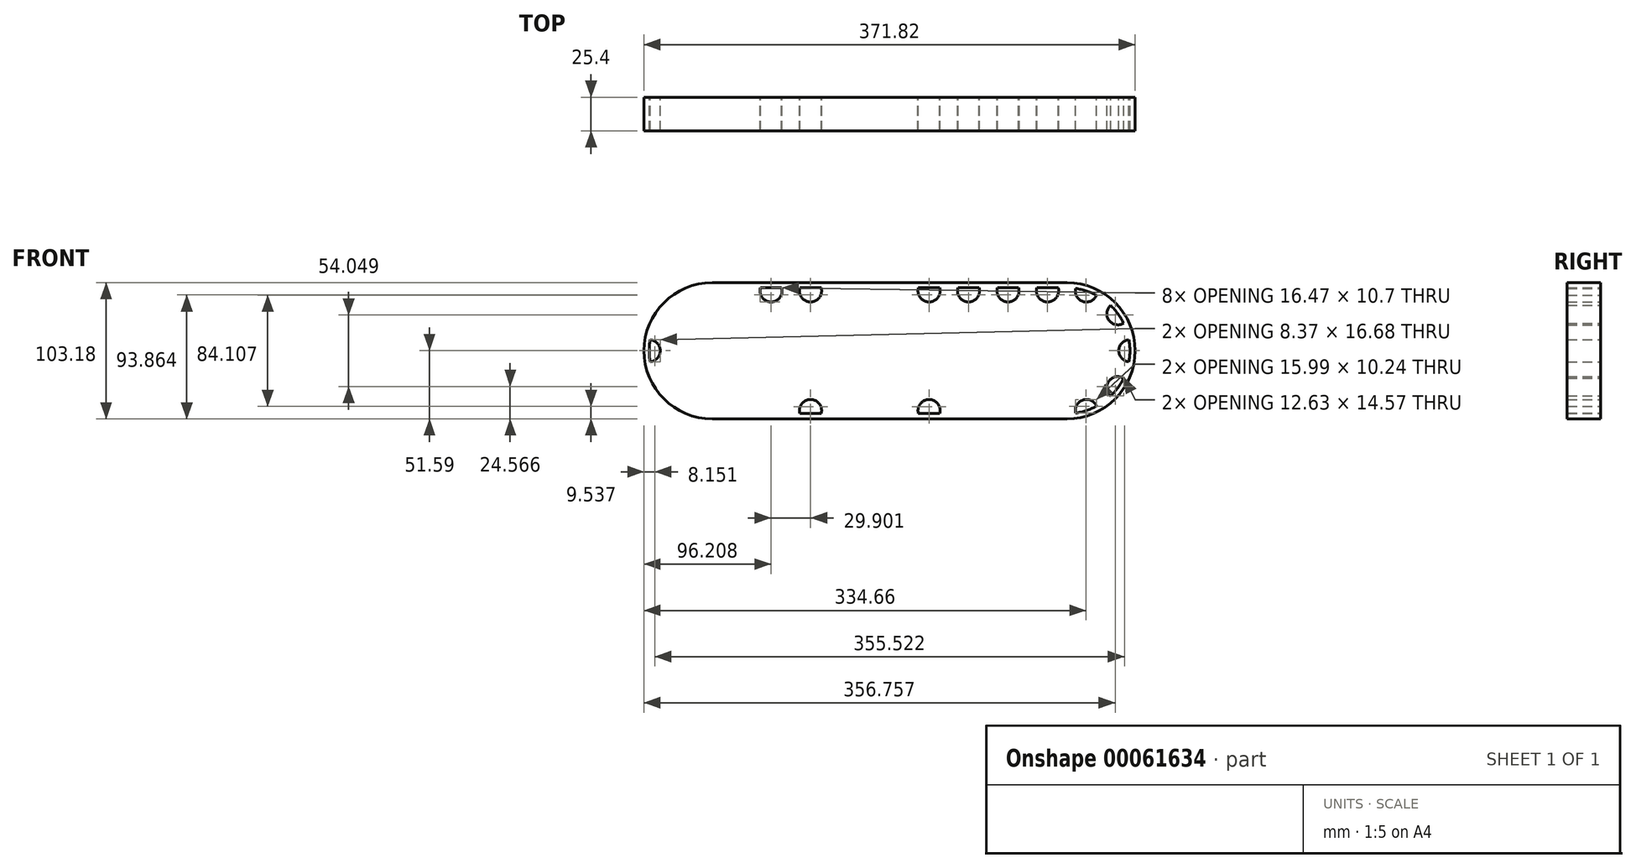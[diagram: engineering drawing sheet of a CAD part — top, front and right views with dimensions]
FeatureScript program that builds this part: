
annotation { "Feature Type Name" : "Feature", "Feature Type Description" : "" }
export const myFeature = defineFeature(function(context is Context, id is Id, definition is map)
    precondition{}
    {
        {
            var Q0;
            Q0=qCreatedBy(makeId("Front.planeOp"),FACE);
            var sketch = newSketch(context, id + "F0", { "sketchPlane" : qUnion([Q0])});
            skCircle(sketch, "E0", {"center": v(0, 0) * mm, "radius": 9.53 * mm});
            skCircle(sketch, "E1", {"center": v(0, 0) * mm, "radius": 15.88 * mm});
            skCircle(sketch, "E2", {"center": v(0, 0) * mm, "radius": 25.4 * mm});
            skCircle(sketch, "E3", {"center": v(0, 0) * mm, "radius": 38.1 * mm});
            skArc(sketch, "E4", {"start": v(5.87, 47.26) * mm, "mid": v(0, 47.63) * mm, "end": v(-5.87, 47.26) * mm});
            skLineSegment(sketch, "E5", {"start": v(-5.87, 47.26) * mm, "end": v(-7.62, 37.33) * mm});
            skLineSegment(sketch, "E6", {"start": v(5.87, 47.26) * mm, "end": v(7.62, 37.33) * mm});
            skLineSegment(sketch, "E7.1.0", {"start": v(-32.53, 34.79) * mm, "end": v(-28.1, 25.72) * mm});
            skArc(sketch, "E7.1.1", {"start": v(-23.03, 41.69) * mm, "mid": v(-28, 38.53) * mm, "end": v(-32.53, 34.79) * mm});
            skLineSegment(sketch, "E7.1.2", {"start": v(-23.03, 41.69) * mm, "end": v(-15.78, 34.68) * mm});
            skLineSegment(sketch, "E7.2.0", {"start": v(-46.76, 9.02) * mm, "end": v(-37.86, 4.29) * mm});
            skArc(sketch, "E7.2.1", {"start": v(-43.14, 20.19) * mm, "mid": v(-45.3, 14.72) * mm, "end": v(-46.76, 9.02) * mm});
            skLineSegment(sketch, "E7.2.2", {"start": v(-43.14, 20.19) * mm, "end": v(-33.15, 18.78) * mm});
            skLineSegment(sketch, "E7.3.0", {"start": v(-43.14, -20.19) * mm, "end": v(-33.15, -18.78) * mm});
            skArc(sketch, "E7.3.1", {"start": v(-46.76, -9.02) * mm, "mid": v(-45.3, -14.72) * mm, "end": v(-43.14, -20.19) * mm});
            skLineSegment(sketch, "E7.3.2", {"start": v(-46.76, -9.02) * mm, "end": v(-37.86, -4.29) * mm});
            skLineSegment(sketch, "E7.4.0", {"start": v(-23.03, -41.69) * mm, "end": v(-15.78, -34.68) * mm});
            skArc(sketch, "E7.4.1", {"start": v(-32.53, -34.79) * mm, "mid": v(-28, -38.53) * mm, "end": v(-23.03, -41.69) * mm});
            skLineSegment(sketch, "E7.4.2", {"start": v(-32.53, -34.79) * mm, "end": v(-28.1, -25.72) * mm});
            skLineSegment(sketch, "E7.5.0", {"start": v(5.87, -47.26) * mm, "end": v(7.62, -37.33) * mm});
            skArc(sketch, "E7.5.1", {"start": v(-5.87, -47.26) * mm, "mid": v(0, -47.63) * mm, "end": v(5.87, -47.26) * mm});
            skLineSegment(sketch, "E7.5.2", {"start": v(-5.87, -47.26) * mm, "end": v(-7.62, -37.33) * mm});
            skLineSegment(sketch, "E7.6.0", {"start": v(32.53, -34.79) * mm, "end": v(28.1, -25.72) * mm});
            skArc(sketch, "E7.6.1", {"start": v(23.03, -41.69) * mm, "mid": v(28, -38.53) * mm, "end": v(32.53, -34.79) * mm});
            skLineSegment(sketch, "E7.6.2", {"start": v(23.03, -41.69) * mm, "end": v(15.78, -34.68) * mm});
            skLineSegment(sketch, "E7.7.0", {"start": v(46.76, -9.02) * mm, "end": v(37.86, -4.29) * mm});
            skArc(sketch, "E7.7.1", {"start": v(43.14, -20.19) * mm, "mid": v(45.3, -14.72) * mm, "end": v(46.76, -9.02) * mm});
            skLineSegment(sketch, "E7.7.2", {"start": v(43.14, -20.19) * mm, "end": v(33.15, -18.78) * mm});
            skLineSegment(sketch, "E7.8.0", {"start": v(43.14, 20.19) * mm, "end": v(33.15, 18.78) * mm});
            skArc(sketch, "E7.8.1", {"start": v(46.76, 9.02) * mm, "mid": v(45.3, 14.72) * mm, "end": v(43.14, 20.19) * mm});
            skLineSegment(sketch, "E7.8.2", {"start": v(46.76, 9.02) * mm, "end": v(37.86, 4.29) * mm});
            skLineSegment(sketch, "E7.9.0", {"start": v(23.03, 41.69) * mm, "end": v(15.78, 34.68) * mm});
            skArc(sketch, "E7.9.1", {"start": v(32.53, 34.79) * mm, "mid": v(28, 38.53) * mm, "end": v(23.03, 41.69) * mm});
            skLineSegment(sketch, "E7.9.2", {"start": v(32.53, 34.79) * mm, "end": v(28.1, 25.72) * mm});
            skLineSegment(sketch, "E8", {"start": v(-3.98, 25.09) * mm, "end": v(-3.98, 15.37) * mm, "construction": true});
            skLineSegment(sketch, "E9", {"start": v(3.98, 25.09) * mm, "end": v(3.98, 15.37) * mm, "construction": true});
            skLineSegment(sketch, "E10.1.0", {"start": v(-19.74, -15.99) * mm, "end": v(-11.32, -11.13) * mm, "construction": true});
            skLineSegment(sketch, "E10.1.1", {"start": v(-23.71, -9.1) * mm, "end": v(-15.3, -4.24) * mm, "construction": true});
            skLineSegment(sketch, "E10.2.0", {"start": v(23.71, -9.1) * mm, "end": v(15.3, -4.24) * mm, "construction": true});
            skLineSegment(sketch, "E10.2.1", {"start": v(19.74, -15.99) * mm, "end": v(11.32, -11.13) * mm, "construction": true});
            skSolve(sketch);
        }
        {
            var Q0;
            Q0=qCreatedBy(makeId("Front.planeOp"),FACE);
            var sketch = newSketch(context, id + "F1", { "sketchPlane" : qUnion([Q0])});
            skArc(sketch, "E11", {"start": v(23.03, 41.69) * mm, "mid": v(-10.34, 46.49) * mm, "end": v(-38.53, 28) * mm});
            skLineSegment(sketch, "E12.0", {"start": v(5.87, 47.26) * mm, "end": v(7.62, 37.33) * mm, "construction": true});
            skLineSegment(sketch, "E12.1", {"start": v(23.03, 41.69) * mm, "end": v(15.78, 34.68) * mm, "construction": true});
            skLineSegment(sketch, "E12.2", {"start": v(-5.87, 47.26) * mm, "end": v(-7.62, 37.33) * mm, "construction": true});
            skLineSegment(sketch, "E12.3", {"start": v(-23.03, 41.69) * mm, "end": v(-15.78, 34.68) * mm, "construction": true});
            skLineSegment(sketch, "E12.4", {"start": v(-32.53, 34.79) * mm, "end": v(-28.1, 25.72) * mm, "construction": true});
            skLineSegment(sketch, "E12.5", {"start": v(-43.14, 20.19) * mm, "end": v(-33.15, 18.78) * mm, "construction": true});
            skLineSegment(sketch, "E12.6", {"start": v(-46.76, 9.02) * mm, "end": v(-37.86, 4.29) * mm, "construction": true});
            skLineSegment(sketch, "E12.7", {"start": v(-46.76, -9.02) * mm, "end": v(-37.86, -4.29) * mm, "construction": true});
            skCircle(sketch, "E13", {"center": v(-14.72, 45.3) * mm, "radius": 8.37 * mm});
            skCircle(sketch, "E14", {"center": v(-38.53, 28) * mm, "radius": 8.37 * mm});
            skCircle(sketch, "E15", {"center": v(-47.63, 0) * mm, "radius": 8.37 * mm});
            skCircle(sketch, "E16", {"center": v(14.72, 45.3) * mm, "radius": 8.37 * mm});
            skLineSegment(sketch, "E17", {"start": v(-14.72, 45.3) * mm, "end": v(14.72, 45.3) * mm, "construction": true});
            skArc(sketch, "E18.trimOffspring", {"start": v(-42.84, 20.81) * mm, "mid": v(-45.3, 14.72) * mm, "end": v(-46.89, 8.34) * mm});
            skArc(sketch, "E19.trimOffspring", {"start": v(-47.63, 0) * mm, "mid": v(-24.2, -41.02) * mm, "end": v(23.03, -41.69) * mm});
            skLineSegment(sketch, "E20", {"start": v(14.72, 45.3) * mm, "end": v(44.62, 45.3) * mm, "construction": true});
            skLineSegment(sketch, "E21", {"start": v(44.62, 45.3) * mm, "end": v(74.52, 45.3) * mm, "construction": true});
            skLineSegment(sketch, "E22", {"start": v(74.52, 45.3) * mm, "end": v(104.42, 45.3) * mm, "construction": true});
            skLineSegment(sketch, "E23", {"start": v(104.42, 45.3) * mm, "end": v(134.32, 45.3) * mm, "construction": true});
            skCircle(sketch, "E24", {"center": v(44.62, 45.3) * mm, "radius": 8.37 * mm});
            skCircle(sketch, "E25", {"center": v(74.52, 45.3) * mm, "radius": 8.37 * mm});
            skCircle(sketch, "E26", {"center": v(104.42, 45.3) * mm, "radius": 8.37 * mm});
            skCircle(sketch, "E27", {"center": v(134.32, 45.3) * mm, "radius": 8.37 * mm});
            skPoint(sketch, "E28", {"position": v(23.09, 45.3) * mm});
            skPoint(sketch, "E29", {"position": v(36.25, 45.3) * mm});
            skLineSegment(sketch, "E30", {"start": v(0, 0) * mm, "end": v(134.32, 0) * mm, "construction": true});
            skLineSegment(sketch, "E31", {"start": v(134.32, 45.3) * mm, "end": v(134.32, 0) * mm, "construction": true});
            skCircle(sketch, "E32.MirrorC", {"center": v(134.32, -45.3) * mm, "radius": 8.37 * mm});
            skCircle(sketch, "E33.MirrorC", {"center": v(104.42, -45.3) * mm, "radius": 8.37 * mm});
            skCircle(sketch, "E34.MirrorC", {"center": v(74.52, -45.3) * mm, "radius": 8.37 * mm});
            skCircle(sketch, "E35.MirrorC", {"center": v(44.62, -45.3) * mm, "radius": 8.37 * mm});
            skCircle(sketch, "E36.MirrorC", {"center": v(14.72, -45.3) * mm, "radius": 8.37 * mm});
            skCircle(sketch, "E37.MirrorC", {"center": v(-14.72, -45.3) * mm, "radius": 8.37 * mm});
            skCircle(sketch, "E38.MirrorC", {"center": v(-38.53, -28) * mm, "radius": 8.37 * mm});
            skCircle(sketch, "E39.MirrorC", {"center": v(164.22, 45.3) * mm, "radius": 8.37 * mm});
            skCircle(sketch, "E40.MirrorC", {"center": v(194.12, 45.3) * mm, "radius": 8.37 * mm});
            skCircle(sketch, "E41.MirrorC", {"center": v(224.03, 45.3) * mm, "radius": 8.37 * mm});
            skCircle(sketch, "E42.MirrorC", {"center": v(253.93, 45.3) * mm, "radius": 8.37 * mm});
            skCircle(sketch, "E43.MirrorC", {"center": v(283.36, 45.3) * mm, "radius": 8.37 * mm});
            skCircle(sketch, "E44.MirrorC", {"center": v(307.17, 28) * mm, "radius": 8.37 * mm});
            skCircle(sketch, "E45.MirrorC", {"center": v(316.27, 0) * mm, "radius": 8.37 * mm});
            skCircle(sketch, "E46.MirrorC", {"center": v(307.17, -28) * mm, "radius": 8.37 * mm});
            skCircle(sketch, "E47.MirrorC", {"center": v(283.36, -45.3) * mm, "radius": 8.37 * mm});
            skCircle(sketch, "E48.MirrorC", {"center": v(253.93, -45.3) * mm, "radius": 8.37 * mm});
            skCircle(sketch, "E49.MirrorC", {"center": v(224.03, -45.3) * mm, "radius": 8.37 * mm});
            skCircle(sketch, "E50.MirrorC", {"center": v(194.12, -45.3) * mm, "radius": 8.37 * mm});
            skCircle(sketch, "E51.MirrorC", {"center": v(164.22, -45.3) * mm, "radius": 8.37 * mm});
            skSolve(sketch);
        }
        {
            var Q0;
            Q0=qCreatedBy(makeId("Front.planeOp"),FACE);
            var sketch = newSketch(context, id + "F2", { "sketchPlane" : qUnion([Q0])});
            skArc(sketch, "E52", {"start": v(0, 47.63) * mm, "mid": v(-47.63, 0) * mm, "end": v(0, -47.63) * mm});
            skLineSegment(sketch, "E53", {"start": v(0, 47.63) * mm, "end": v(268.64, 47.63) * mm});
            skLineSegment(sketch, "E54", {"start": v(0, -47.63) * mm, "end": v(268.64, -47.63) * mm});
            skLineSegment(sketch, "E55.0", {"start": v(0, 0) * mm, "end": v(134.32, 0) * mm, "construction": true});
            skLineSegment(sketch, "E56.0", {"start": v(134.32, 45.3) * mm, "end": v(134.32, 0) * mm, "construction": true});
            skLineSegment(sketch, "E57.MirrorCS", {"start": v(268.64, 0) * mm, "end": v(134.32, 0) * mm, "construction": true});
            skArc(sketch, "E58", {"start": v(268.64, 47.62) * mm, "mid": v(316.27, 0) * mm, "end": v(268.64, -47.63) * mm});
            skLineSegment(sketch, "E59.0", {"start": v(0, 51.59) * mm, "end": v(268.64, 51.59) * mm});
            skArc(sketch, "E59.1", {"start": v(0, 51.59) * mm, "mid": v(-51.59, 0) * mm, "end": v(0, -51.59) * mm});
            skLineSegment(sketch, "E59.2", {"start": v(0, -51.59) * mm, "end": v(268.64, -51.59) * mm});
            skArc(sketch, "E59.3", {"start": v(268.64, 51.59) * mm, "mid": v(320.23, 0) * mm, "end": v(268.64, -51.59) * mm});
            skArc(sketch, "E60.0", {"start": v(-23.04, 46.15) * mm, "mid": v(-12.13, 37.33) * mm, "end": v(-8.49, 50.88) * mm});
            skArc(sketch, "E60.1", {"start": v(9.2, 51.59) * mm, "mid": v(14.72, 36.92) * mm, "end": v(20.24, 51.59) * mm});
            skArc(sketch, "E60.2", {"start": v(39.1, 51.59) * mm, "mid": v(44.62, 36.92) * mm, "end": v(50.14, 51.59) * mm});
            skArc(sketch, "E60.3", {"start": v(69, 51.59) * mm, "mid": v(74.52, 36.92) * mm, "end": v(80.04, 51.59) * mm});
            skArc(sketch, "E60.4", {"start": v(98.9, 51.59) * mm, "mid": v(102.07, 37.26) * mm, "end": v(112.46, 47.63) * mm});
            skArc(sketch, "E60.5", {"start": v(128.8, 51.59) * mm, "mid": v(134.32, 36.92) * mm, "end": v(139.84, 51.59) * mm});
            skArc(sketch, "E60.6", {"start": v(169.74, 51.59) * mm, "mid": v(164.22, 36.92) * mm, "end": v(158.7, 51.59) * mm});
            skArc(sketch, "E60.7", {"start": v(199.65, 51.59) * mm, "mid": v(194.12, 36.92) * mm, "end": v(188.6, 51.59) * mm});
            skArc(sketch, "E60.8", {"start": v(229.55, 51.59) * mm, "mid": v(224.03, 36.92) * mm, "end": v(218.5, 51.59) * mm});
            skArc(sketch, "E60.9", {"start": v(259.45, 51.59) * mm, "mid": v(253.93, 36.92) * mm, "end": v(248.4, 51.59) * mm});
            skArc(sketch, "E60.10", {"start": v(-45.77, 23.8) * mm, "mid": v(-31.76, 23.07) * mm, "end": v(-36.77, 36.18) * mm});
            skArc(sketch, "E60.11", {"start": v(-51.02, -7.65) * mm, "mid": v(-39.25, 0) * mm, "end": v(-51.02, 7.65) * mm});
            skArc(sketch, "E60.12", {"start": v(-45.77, -23.8) * mm, "mid": v(-31.76, -23.07) * mm, "end": v(-36.77, -36.18) * mm});
            skArc(sketch, "E60.13", {"start": v(-23.04, -46.15) * mm, "mid": v(-12.13, -37.33) * mm, "end": v(-8.49, -50.88) * mm});
            skArc(sketch, "E60.14", {"start": v(9.2, -51.59) * mm, "mid": v(14.72, -36.92) * mm, "end": v(20.24, -51.59) * mm});
            skArc(sketch, "E60.15", {"start": v(39.1, -51.59) * mm, "mid": v(44.62, -36.92) * mm, "end": v(50.14, -51.59) * mm});
            skArc(sketch, "E60.16", {"start": v(69, -51.59) * mm, "mid": v(74.52, -36.92) * mm, "end": v(80.04, -51.59) * mm});
            skArc(sketch, "E60.17", {"start": v(98.9, -51.59) * mm, "mid": v(104.42, -36.92) * mm, "end": v(109.94, -51.59) * mm});
            skArc(sketch, "E60.18", {"start": v(169.74, -51.59) * mm, "mid": v(164.22, -36.92) * mm, "end": v(158.7, -51.59) * mm});
            skArc(sketch, "E60.19", {"start": v(128.8, -51.59) * mm, "mid": v(134.32, -36.92) * mm, "end": v(139.84, -51.59) * mm});
            skArc(sketch, "E60.20", {"start": v(199.65, -51.59) * mm, "mid": v(194.12, -36.92) * mm, "end": v(188.6, -51.59) * mm});
            skArc(sketch, "E60.21", {"start": v(229.55, -51.59) * mm, "mid": v(224.03, -36.92) * mm, "end": v(218.5, -51.59) * mm});
            skArc(sketch, "E60.22", {"start": v(259.45, -51.59) * mm, "mid": v(253.93, -36.92) * mm, "end": v(248.4, -51.59) * mm});
            skArc(sketch, "E60.23", {"start": v(291.06, -42.02) * mm, "mid": v(278.87, -38.23) * mm, "end": v(277.13, -50.88) * mm});
            skArc(sketch, "E60.24", {"start": v(319.66, -7.65) * mm, "mid": v(307.9, 0) * mm, "end": v(319.66, 7.65) * mm});
            skArc(sketch, "E60.25", {"start": v(314.42, 23.8) * mm, "mid": v(300.4, 23.07) * mm, "end": v(305.42, 36.18) * mm});
            skArc(sketch, "E60.26", {"start": v(291.69, 46.15) * mm, "mid": v(280.77, 37.33) * mm, "end": v(277.13, 50.88) * mm});
            skArc(sketch, "E61.0", {"start": v(314.42, -23.8) * mm, "mid": v(300.4, -23.07) * mm, "end": v(305.42, -36.18) * mm});
            skSolve(sketch);
        }
        {
            var Q0;
            Q0 = qSketchRegion(id + "F2", true);
            var Q1;
            {var subQ0=sQuery(id+"F2.wireOp",EDGE,"E60.11");var subQ1=sQuery(id+"F2.wireOp",EDGE,"E52");var subQ2=makeQuery(id+"F2.imprint","INTERSECT",VERTEX,{"disambiguationData":[OD(0.0)],"derivedFrom":[subQ1,subQ0]});Q1=makeQuery(id+"F2.imprint","IMPRINT",FACE,{"disambiguationData":[TD([[makeQuery(id+"F2.imprint","IMPRINT",EDGE,{"disambiguationData":[TD([[subQ2,-1.0]])],"derivedFrom":subQ1}),1.0]])]});}
            var Q2;
            {var subQ0=sQuery(id+"F2.wireOp",EDGE,"E60.12");var subQ1=sQuery(id+"F2.wireOp",EDGE,"E52");var subQ2=makeQuery(id+"F2.imprint","INTERSECT",VERTEX,{"disambiguationData":[OD(0.0)],"derivedFrom":[subQ1,subQ0]});Q2=makeQuery(id+"F2.imprint","IMPRINT",FACE,{"disambiguationData":[TD([[makeQuery(id+"F2.imprint","IMPRINT",EDGE,{"disambiguationData":[TD([[subQ2,-1.0]])],"derivedFrom":subQ1}),1.0]])]});}
            var Q3;
            {var subQ0=sQuery(id+"F2.wireOp",EDGE,"E60.13");var subQ1=sQuery(id+"F2.wireOp",EDGE,"E52");var subQ2=makeQuery(id+"F2.imprint","INTERSECT",VERTEX,{"disambiguationData":[OD(0.0)],"derivedFrom":[subQ1,subQ0]});Q3=makeQuery(id+"F2.imprint","IMPRINT",FACE,{"disambiguationData":[TD([[makeQuery(id+"F2.imprint","IMPRINT",EDGE,{"disambiguationData":[TD([[subQ2,-1.0]])],"derivedFrom":subQ1}),1.0]])]});}
            var Q4;
            {var subQ0=sQuery(id+"F2.wireOp",EDGE,"E60.14");var subQ1=sQuery(id+"F2.wireOp",EDGE,"E54");var subQ2=makeQuery(id+"F2.imprint","INTERSECT",VERTEX,{"disambiguationData":[OD(0.0)],"derivedFrom":[subQ1,subQ0]});Q4=makeQuery(id+"F2.imprint","IMPRINT",FACE,{"disambiguationData":[TD([[makeQuery(id+"F2.imprint","IMPRINT",EDGE,{"disambiguationData":[TD([[subQ2,-1.0]])],"derivedFrom":subQ1}),1.0]])]});}
            var Q5;
            {var subQ0=sQuery(id+"F2.wireOp",EDGE,"E60.15");var subQ1=sQuery(id+"F2.wireOp",EDGE,"E54");var subQ2=makeQuery(id+"F2.imprint","INTERSECT",VERTEX,{"disambiguationData":[OD(0.0)],"derivedFrom":[subQ1,subQ0]});Q5=makeQuery(id+"F2.imprint","IMPRINT",FACE,{"disambiguationData":[TD([[makeQuery(id+"F2.imprint","IMPRINT",EDGE,{"disambiguationData":[TD([[subQ2,-1.0]])],"derivedFrom":subQ1}),1.0]])]});}
            var Q6;
            {var subQ0=sQuery(id+"F2.wireOp",EDGE,"E60.16");var subQ1=sQuery(id+"F2.wireOp",EDGE,"E54");var subQ2=makeQuery(id+"F2.imprint","INTERSECT",VERTEX,{"disambiguationData":[OD(0.0)],"derivedFrom":[subQ1,subQ0]});Q6=makeQuery(id+"F2.imprint","IMPRINT",FACE,{"disambiguationData":[TD([[makeQuery(id+"F2.imprint","IMPRINT",EDGE,{"disambiguationData":[TD([[subQ2,-1.0]])],"derivedFrom":subQ1}),1.0]])]});}
            var Q7;
            {var subQ0=sQuery(id+"F2.wireOp",EDGE,"E60.17");var subQ1=sQuery(id+"F2.wireOp",EDGE,"E54");var subQ2=makeQuery(id+"F2.imprint","INTERSECT",VERTEX,{"disambiguationData":[OD(0.0)],"derivedFrom":[subQ1,subQ0]});Q7=makeQuery(id+"F2.imprint","IMPRINT",FACE,{"disambiguationData":[TD([[makeQuery(id+"F2.imprint","IMPRINT",EDGE,{"disambiguationData":[TD([[subQ2,-1.0]])],"derivedFrom":subQ1}),1.0]])]});}
            var Q8;
            {var subQ0=sQuery(id+"F2.wireOp",EDGE,"E60.19");var subQ1=sQuery(id+"F2.wireOp",EDGE,"E54");var subQ2=makeQuery(id+"F2.imprint","INTERSECT",VERTEX,{"disambiguationData":[OD(0.0)],"derivedFrom":[subQ1,subQ0]});Q8=makeQuery(id+"F2.imprint","IMPRINT",FACE,{"disambiguationData":[TD([[makeQuery(id+"F2.imprint","IMPRINT",EDGE,{"disambiguationData":[TD([[subQ2,-1.0]])],"derivedFrom":subQ1}),1.0]])]});}
            var Q9;
            {var subQ0=sQuery(id+"F2.wireOp",EDGE,"E60.18");var subQ1=sQuery(id+"F2.wireOp",EDGE,"E54");var subQ2=makeQuery(id+"F2.imprint","INTERSECT",VERTEX,{"disambiguationData":[OD(0.0)],"derivedFrom":[subQ1,subQ0]});Q9=makeQuery(id+"F2.imprint","IMPRINT",FACE,{"disambiguationData":[TD([[makeQuery(id+"F2.imprint","IMPRINT",EDGE,{"disambiguationData":[TD([[subQ2,-1.0]])],"derivedFrom":subQ1}),1.0]])]});}
            var Q10;
            {var subQ0=sQuery(id+"F2.wireOp",EDGE,"E60.20");var subQ1=sQuery(id+"F2.wireOp",EDGE,"E54");var subQ2=makeQuery(id+"F2.imprint","INTERSECT",VERTEX,{"disambiguationData":[OD(0.0)],"derivedFrom":[subQ1,subQ0]});Q10=makeQuery(id+"F2.imprint","IMPRINT",FACE,{"disambiguationData":[TD([[makeQuery(id+"F2.imprint","IMPRINT",EDGE,{"disambiguationData":[TD([[subQ2,-1.0]])],"derivedFrom":subQ1}),1.0]])]});}
            var Q11;
            {var subQ0=sQuery(id+"F2.wireOp",EDGE,"E60.21");var subQ1=sQuery(id+"F2.wireOp",EDGE,"E54");var subQ2=makeQuery(id+"F2.imprint","INTERSECT",VERTEX,{"disambiguationData":[OD(0.0)],"derivedFrom":[subQ1,subQ0]});Q11=makeQuery(id+"F2.imprint","IMPRINT",FACE,{"disambiguationData":[TD([[makeQuery(id+"F2.imprint","IMPRINT",EDGE,{"disambiguationData":[TD([[subQ2,-1.0]])],"derivedFrom":subQ1}),1.0]])]});}
            var Q12;
            {var subQ0=sQuery(id+"F2.wireOp",EDGE,"E60.22");var subQ1=sQuery(id+"F2.wireOp",EDGE,"E54");var subQ2=makeQuery(id+"F2.imprint","INTERSECT",VERTEX,{"disambiguationData":[OD(0.0)],"derivedFrom":[subQ1,subQ0]});Q12=makeQuery(id+"F2.imprint","IMPRINT",FACE,{"disambiguationData":[TD([[makeQuery(id+"F2.imprint","IMPRINT",EDGE,{"disambiguationData":[TD([[subQ2,-1.0]])],"derivedFrom":subQ1}),1.0]])]});}
            var Q13;
            {var subQ0=sQuery(id+"F2.wireOp",EDGE,"E60.23");var subQ1=sQuery(id+"F2.wireOp",EDGE,"E58");var subQ2=makeQuery(id+"F2.imprint","INTERSECT",VERTEX,{"disambiguationData":[OD(0.0)],"derivedFrom":[subQ1,subQ0]});Q13=makeQuery(id+"F2.imprint","IMPRINT",FACE,{"disambiguationData":[TD([[makeQuery(id+"F2.imprint","IMPRINT",EDGE,{"disambiguationData":[TD([[subQ2,-1.0]])],"derivedFrom":subQ1}),-1.0]])]});}
            var Q14;
            {var subQ0=sQuery(id+"F2.wireOp",EDGE,"E60.24");var subQ1=sQuery(id+"F2.wireOp",EDGE,"E58");var subQ2=makeQuery(id+"F2.imprint","INTERSECT",VERTEX,{"disambiguationData":[OD(0.0)],"derivedFrom":[subQ1,subQ0]});Q14=makeQuery(id+"F2.imprint","IMPRINT",FACE,{"disambiguationData":[TD([[makeQuery(id+"F2.imprint","IMPRINT",EDGE,{"disambiguationData":[TD([[subQ2,-1.0]])],"derivedFrom":subQ1}),-1.0]])]});}
            var Q15;
            {var subQ0=sQuery(id+"F2.wireOp",EDGE,"E60.25");var subQ1=sQuery(id+"F2.wireOp",EDGE,"E58");var subQ2=makeQuery(id+"F2.imprint","INTERSECT",VERTEX,{"disambiguationData":[OD(0.0)],"derivedFrom":[subQ1,subQ0]});Q15=makeQuery(id+"F2.imprint","IMPRINT",FACE,{"disambiguationData":[TD([[makeQuery(id+"F2.imprint","IMPRINT",EDGE,{"disambiguationData":[TD([[subQ2,-1.0]])],"derivedFrom":subQ1}),-1.0]])]});}
            var Q16;
            {var subQ0=sQuery(id+"F2.wireOp",EDGE,"E60.26");var subQ1=sQuery(id+"F2.wireOp",EDGE,"E58");var subQ2=makeQuery(id+"F2.imprint","INTERSECT",VERTEX,{"disambiguationData":[OD(0.0)],"derivedFrom":[subQ1,subQ0]});Q16=makeQuery(id+"F2.imprint","IMPRINT",FACE,{"disambiguationData":[TD([[makeQuery(id+"F2.imprint","IMPRINT",EDGE,{"disambiguationData":[TD([[subQ2,-1.0]])],"derivedFrom":subQ1}),-1.0]])]});}
            var Q17;
            {var subQ0=sQuery(id+"F2.wireOp",EDGE,"E60.9");var subQ1=sQuery(id+"F2.wireOp",EDGE,"E53");var subQ2=makeQuery(id+"F2.imprint","INTERSECT",VERTEX,{"disambiguationData":[OD(0.0)],"derivedFrom":[subQ1,subQ0]});Q17=makeQuery(id+"F2.imprint","IMPRINT",FACE,{"disambiguationData":[TD([[makeQuery(id+"F2.imprint","IMPRINT",EDGE,{"disambiguationData":[TD([[subQ2,-1.0]])],"derivedFrom":subQ1}),-1.0]])]});}
            var Q18;
            {var subQ0=sQuery(id+"F2.wireOp",EDGE,"E60.8");var subQ1=sQuery(id+"F2.wireOp",EDGE,"E53");var subQ2=makeQuery(id+"F2.imprint","INTERSECT",VERTEX,{"disambiguationData":[OD(0.0)],"derivedFrom":[subQ1,subQ0]});Q18=makeQuery(id+"F2.imprint","IMPRINT",FACE,{"disambiguationData":[TD([[makeQuery(id+"F2.imprint","IMPRINT",EDGE,{"disambiguationData":[TD([[subQ2,-1.0]])],"derivedFrom":subQ1}),-1.0]])]});}
            var Q19;
            {var subQ0=sQuery(id+"F2.wireOp",EDGE,"E60.7");var subQ1=sQuery(id+"F2.wireOp",EDGE,"E53");var subQ2=makeQuery(id+"F2.imprint","INTERSECT",VERTEX,{"disambiguationData":[OD(0.0)],"derivedFrom":[subQ1,subQ0]});Q19=makeQuery(id+"F2.imprint","IMPRINT",FACE,{"disambiguationData":[TD([[makeQuery(id+"F2.imprint","IMPRINT",EDGE,{"disambiguationData":[TD([[subQ2,-1.0]])],"derivedFrom":subQ1}),-1.0]])]});}
            var Q20;
            {var subQ0=sQuery(id+"F2.wireOp",EDGE,"E60.6");var subQ1=sQuery(id+"F2.wireOp",EDGE,"E53");var subQ2=makeQuery(id+"F2.imprint","INTERSECT",VERTEX,{"disambiguationData":[OD(0.0)],"derivedFrom":[subQ1,subQ0]});Q20=makeQuery(id+"F2.imprint","IMPRINT",FACE,{"disambiguationData":[TD([[makeQuery(id+"F2.imprint","IMPRINT",EDGE,{"disambiguationData":[TD([[subQ2,-1.0]])],"derivedFrom":subQ1}),-1.0]])]});}
            var Q21;
            {var subQ0=sQuery(id+"F2.wireOp",EDGE,"E60.5");var subQ1=sQuery(id+"F2.wireOp",EDGE,"E53");var subQ2=makeQuery(id+"F2.imprint","INTERSECT",VERTEX,{"disambiguationData":[OD(0.0)],"derivedFrom":[subQ1,subQ0]});Q21=makeQuery(id+"F2.imprint","IMPRINT",FACE,{"disambiguationData":[TD([[makeQuery(id+"F2.imprint","IMPRINT",EDGE,{"disambiguationData":[TD([[subQ2,-1.0]])],"derivedFrom":subQ1}),-1.0]])]});}
            var Q22;
            {var subQ0=sQuery(id+"F2.wireOp",EDGE,"E60.4");var subQ1=sQuery(id+"F2.wireOp",EDGE,"E53");var subQ2=makeQuery(id+"F2.imprint","INTERSECT",VERTEX,{"disambiguationData":[OD(0.0)],"derivedFrom":[subQ1,subQ0]});Q22=makeQuery(id+"F2.imprint","IMPRINT",FACE,{"disambiguationData":[TD([[makeQuery(id+"F2.imprint","IMPRINT",EDGE,{"disambiguationData":[TD([[subQ2,1.0]])],"derivedFrom":subQ1}),-1.0]])]});}
            var Q23;
            {var subQ0=sQuery(id+"F2.wireOp",EDGE,"E60.3");var subQ1=sQuery(id+"F2.wireOp",EDGE,"E53");var subQ2=makeQuery(id+"F2.imprint","INTERSECT",VERTEX,{"disambiguationData":[OD(0.0)],"derivedFrom":[subQ1,subQ0]});Q23=makeQuery(id+"F2.imprint","IMPRINT",FACE,{"disambiguationData":[TD([[makeQuery(id+"F2.imprint","IMPRINT",EDGE,{"disambiguationData":[TD([[subQ2,-1.0]])],"derivedFrom":subQ1}),-1.0]])]});}
            var Q24;
            {var subQ0=sQuery(id+"F2.wireOp",EDGE,"E60.2");var subQ1=sQuery(id+"F2.wireOp",EDGE,"E53");var subQ2=makeQuery(id+"F2.imprint","INTERSECT",VERTEX,{"disambiguationData":[OD(0.0)],"derivedFrom":[subQ1,subQ0]});Q24=makeQuery(id+"F2.imprint","IMPRINT",FACE,{"disambiguationData":[TD([[makeQuery(id+"F2.imprint","IMPRINT",EDGE,{"disambiguationData":[TD([[subQ2,-1.0]])],"derivedFrom":subQ1}),-1.0]])]});}
            var Q25;
            {var subQ0=sQuery(id+"F2.wireOp",EDGE,"E60.1");var subQ1=sQuery(id+"F2.wireOp",EDGE,"E53");var subQ2=makeQuery(id+"F2.imprint","INTERSECT",VERTEX,{"disambiguationData":[OD(0.0)],"derivedFrom":[subQ1,subQ0]});Q25=makeQuery(id+"F2.imprint","IMPRINT",FACE,{"disambiguationData":[TD([[makeQuery(id+"F2.imprint","IMPRINT",EDGE,{"disambiguationData":[TD([[subQ2,-1.0]])],"derivedFrom":subQ1}),-1.0]])]});}
            var Q26;
            {var subQ0=sQuery(id+"F2.wireOp",EDGE,"E60.0");var subQ1=sQuery(id+"F2.wireOp",EDGE,"E52");var subQ2=makeQuery(id+"F2.imprint","INTERSECT",VERTEX,{"disambiguationData":[OD(0.0)],"derivedFrom":[subQ1,subQ0]});Q26=makeQuery(id+"F2.imprint","IMPRINT",FACE,{"disambiguationData":[TD([[makeQuery(id+"F2.imprint","IMPRINT",EDGE,{"disambiguationData":[TD([[subQ2,-1.0]])],"derivedFrom":subQ1}),1.0]])]});}
            var Q27;
            {var subQ0=sQuery(id+"F2.wireOp",EDGE,"E60.10");var subQ1=sQuery(id+"F2.wireOp",EDGE,"E52");var subQ2=makeQuery(id+"F2.imprint","INTERSECT",VERTEX,{"disambiguationData":[OD(0.0)],"derivedFrom":[subQ1,subQ0]});Q27=makeQuery(id+"F2.imprint","IMPRINT",FACE,{"disambiguationData":[TD([[makeQuery(id+"F2.imprint","IMPRINT",EDGE,{"disambiguationData":[TD([[subQ2,-1.0]])],"derivedFrom":subQ1}),1.0]])]});}
            var Q28;
            {var subQ0=sQuery(id+"F2.wireOp",EDGE,"E61.0");var subQ1=sQuery(id+"F2.wireOp",EDGE,"E58");var subQ2=makeQuery(id+"F2.imprint","INTERSECT",VERTEX,{"disambiguationData":[OD(0.0)],"derivedFrom":[subQ1,subQ0]});Q28=makeQuery(id+"F2.imprint","IMPRINT",FACE,{"disambiguationData":[TD([[makeQuery(id+"F2.imprint","IMPRINT",EDGE,{"disambiguationData":[TD([[subQ2,-1.0]])],"derivedFrom":subQ1}),-1.0]])]});}
            extrude(context, id + "F3", {"entities" : qUnion([Q0, Q1, Q2, Q3, Q4, Q5, Q6, Q7, Q8, Q9, Q10, Q11, Q12, Q13, Q14, Q15, Q16, Q17, Q18, Q19, Q20, Q21, Q22, Q23, Q24, Q25, Q26, Q27, Q28]), "depth" : 25.4 * mm});
        }
    });
